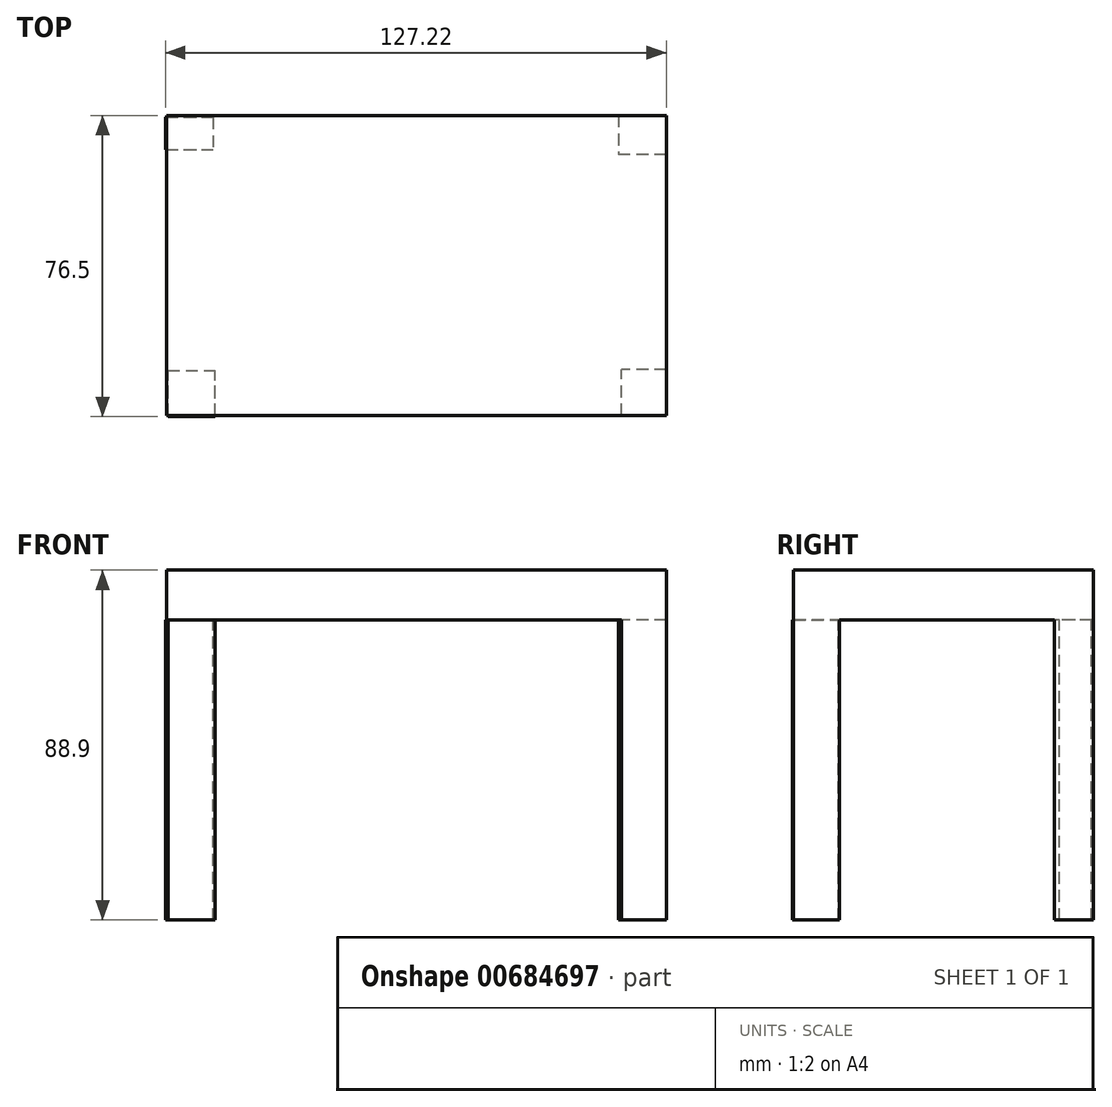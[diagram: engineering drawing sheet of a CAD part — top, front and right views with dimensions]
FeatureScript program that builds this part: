
annotation { "Feature Type Name" : "Feature", "Feature Type Description" : "" }
export const myFeature = defineFeature(function(context is Context, id is Id, definition is map)
    precondition{}
    {
        {
            var Q0;
            Q0=qCreatedBy(makeId("Top.planeOp"),FACE);
            var sketch = newSketch(context, id + "F0", { "sketchPlane" : qUnion([Q0])});
            skLineSegment(sketch, "E0.bottom", {"start": v(-63.35, 18.66) * mm, "end": v(63.65, 18.66) * mm});
            skLineSegment(sketch, "E0.top", {"start": v(-63.35, -57.54) * mm, "end": v(63.65, -57.54) * mm});
            skLineSegment(sketch, "E0.left", {"start": v(-63.35, 18.66) * mm, "end": v(-63.35, -57.54) * mm});
            skLineSegment(sketch, "E0.right", {"start": v(63.65, 18.66) * mm, "end": v(63.65, -57.54) * mm});
            skSolve(sketch);
        }
        {
            var Q0;
            Q0=qSketchRegion(id+"F0",true);
            extrude(context, id + "F1", {"entities" : qUnion([Q0]), "depth" : 12.7 * mm, "offsetDistance" : 25.4 * mm});
        }
        {
            var Q0;
            Q0=qCreatedBy(makeId("Top.planeOp"),FACE);
            var sketch = newSketch(context, id + "F2", { "sketchPlane" : qUnion([Q0])});
            skLineSegment(sketch, "E1.bottom", {"start": v(-62.98, -57.84) * mm, "end": v(-50.94, -57.84) * mm});
            skLineSegment(sketch, "E1.top", {"start": v(-62.98, -46.1) * mm, "end": v(-50.94, -46.1) * mm});
            skLineSegment(sketch, "E1.left", {"start": v(-62.98, -57.84) * mm, "end": v(-62.98, -46.1) * mm});
            skLineSegment(sketch, "E1.right", {"start": v(-50.94, -57.84) * mm, "end": v(-50.94, -46.1) * mm});
            skLineSegment(sketch, "E2.bottom", {"start": v(-63.57, 18.2) * mm, "end": v(-51.53, 18.2) * mm});
            skLineSegment(sketch, "E2.top", {"start": v(-63.57, 9.98) * mm, "end": v(-51.53, 9.98) * mm});
            skLineSegment(sketch, "E2.left", {"start": v(-63.57, 18.2) * mm, "end": v(-63.57, 9.98) * mm});
            skLineSegment(sketch, "E2.right", {"start": v(-51.53, 18.2) * mm, "end": v(-51.53, 9.98) * mm});
            skSolve(sketch);
        }
        {
            var Q0;
            Q0=makeQuery(id+"F1.opExtrude","CAP_FACE",FACE,{"disambiguationData":[OSD([sQuery(id+"F0.wireOp",EDGE,"E0.bottom"),sQuery(id+"F0.wireOp",EDGE,"E0.top"),sQuery(id+"F0.wireOp",EDGE,"E0.left"),sQuery(id+"F0.wireOp",EDGE,"E0.right")])],"isStart":true});
            var sketch = newSketch(context, id + "F3", { "sketchPlane" : qUnion([Q0])});
            skLineSegment(sketch, "E3.bottom", {"start": v(63.65, 57.54) * mm, "end": v(52.24, 57.54) * mm});
            skLineSegment(sketch, "E3.top", {"start": v(63.65, 45.87) * mm, "end": v(52.24, 45.87) * mm});
            skLineSegment(sketch, "E3.left", {"start": v(63.65, 57.54) * mm, "end": v(63.65, 45.87) * mm});
            skLineSegment(sketch, "E3.right", {"start": v(52.24, 57.54) * mm, "end": v(52.24, 45.87) * mm});
            skLineSegment(sketch, "E4.bottom", {"start": v(63.65, -18.66) * mm, "end": v(51.5, -18.66) * mm});
            skLineSegment(sketch, "E4.top", {"start": v(63.65, -8.7) * mm, "end": v(51.5, -8.7) * mm});
            skLineSegment(sketch, "E4.left", {"start": v(63.65, -18.66) * mm, "end": v(63.65, -8.7) * mm});
            skLineSegment(sketch, "E4.right", {"start": v(51.5, -18.66) * mm, "end": v(51.5, -8.7) * mm});
            skSolve(sketch);
        }
        {
            var Q0;
            Q0=qSketchRegion(id+"F3",true);
            extrude(context, id + "F4", {"entities" : qUnion([Q0]), "operationType" : NewBodyOperationType.ADD, "depth" : 76.2 * mm, "offsetDistance" : 25.4 * mm});
        }
        {
            var Q0;
            Q0=qSketchRegion(id+"F2",true);
            extrude(context, id + "F5", {"entities" : qUnion([Q0]), "operationType" : NewBodyOperationType.ADD, "oppositeDirection" : true, "depth" : 76.2 * mm, "offsetDistance" : 25.4 * mm});
        }
    });
